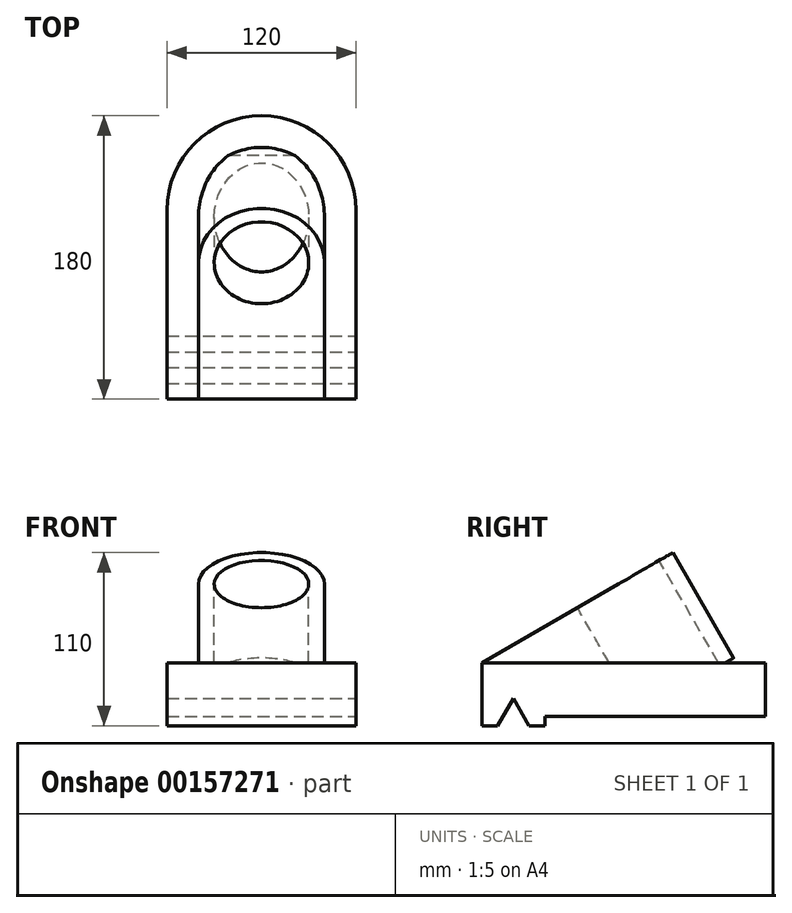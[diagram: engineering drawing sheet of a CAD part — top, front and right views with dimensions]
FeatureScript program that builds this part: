
annotation { "Feature Type Name" : "Feature", "Feature Type Description" : "" }
export const myFeature = defineFeature(function(context is Context, id is Id, definition is map)
    precondition{}
    {
        {
            var Q0;
            Q0=qCreatedBy(makeId("Front.planeOp"),FACE);
            var sketch = newSketch(context, id + "F0", { "sketchPlane" : qUnion([Q0])});
            skLineSegment(sketch, "E0", {"start": v(60, -20) * mm, "end": v(-60, -20) * mm});
            skLineSegment(sketch, "E1", {"start": v(-60, -20) * mm, "end": v(-60, 20) * mm});
            skLineSegment(sketch, "E2", {"start": v(-60, 20) * mm, "end": v(60, 20) * mm});
            skLineSegment(sketch, "E3", {"start": v(60, 20) * mm, "end": v(60, -20) * mm});
            skPoint(sketch, "E4.start.orphan", {"position": v(68, 0) * mm});
            skPoint(sketch, "E5.orphan", {"position": v(68, -20) * mm});
            skSolve(sketch);
        }
        {
            var Q0;
            Q0=makeQuery(id+"F0.imprint","IMPRINT",FACE,{"disambiguationData":[TD([[makeQuery(id+"F0.imprint","IMPRINT",EDGE,{"derivedFrom":sQuery(id+"F0.wireOp",EDGE,"E0")}),-1.0]])]});
            extrude(context, id + "F1", {"entities" : qUnion([Q0]), "oppositeDirection" : true, "depth" : 120 * mm});
        }
        {
            var Q0;
            Q0=makeQuery(id+"F1.opExtrude","SWEPT_FACE",FACE,{"disambiguationData":[OSD([sQuery(id+"F0.wireOp",EDGE,"E2")])]});
            var sketch = newSketch(context, id + "F2", { "sketchPlane" : qUnion([Q0])});
            skArc(sketch, "E6", {"start": v(60, 120) * mm, "mid": v(0, 180) * mm, "end": v(-60, 120) * mm});
            skSolve(sketch);
        }
        {
            var Q0;
            Q0=makeQuery(id+"F2.imprint","IMPRINT",FACE,{"disambiguationData":[TD([[makeQuery(id+"F2.imprint","IMPRINT",EDGE,{"derivedFrom":sQuery(id+"F2.wireOp",EDGE,"E6")}),1.0]])]});
            extrude(context, id + "F3", {"entities" : qUnion([Q0]), "operationType" : NewBodyOperationType.ADD, "oppositeDirection" : true, "depth" : 40 * mm});
        }
        {
            var Q0;
            Q0=makeQuery(id+"F1.opExtrude","CAP_EDGE",EDGE,{"disambiguationData":[OSD([sQuery(id+"F0.wireOp",EDGE,"E2")])],"isStart":true});
            cPlane(context, id + "F4", {"entities" : qUnion([Q0]), "cplaneType" : CPlaneType.LINE_ANGLE, "offset" : 25 * mm, "angle" : 120 * degree, "width" : 150 * mm, "height" : 150 * mm});
        }
        {
            var Q0;
            Q0=qCreatedBy(id+"F4.planeOp",FACE);
            var sketch = newSketch(context, id + "F5", { "sketchPlane" : qUnion([Q0])});
            skLineSegment(sketch, "E7", {"start": v(0, 10) * mm, "end": v(40, 10) * mm});
            skLineSegment(sketch, "E8", {"start": v(40, 10) * mm, "end": v(40, 110) * mm});
            skLineSegment(sketch, "E9", {"start": v(-40, 110) * mm, "end": v(-40, 10) * mm});
            skLineSegment(sketch, "E10", {"start": v(-40, 10) * mm, "end": v(0, 10) * mm});
            skCircle(sketch, "E11", {"center": v(0, 110) * mm, "radius": 40 * mm});
            skCircle(sketch, "E12", {"center": v(0, 110) * mm, "radius": 30 * mm});
            skSolve(sketch);
        }
        {
            var Q0;
            Q0=makeQuery(id+"F5.imprint","IMPRINT",FACE,{"disambiguationData":[TD([[makeQuery(id+"F5.imprint","IMPRINT",EDGE,{"derivedFrom":sQuery(id+"F5.wireOp",EDGE,"E7")}),1.0]])]});
            var Q1;
            Q1=makeQuery(id+"F5.imprint","IMPRINT",FACE,{"disambiguationData":[TD([[makeQuery(id+"F5.imprint","IMPRINT",EDGE,{"derivedFrom":sQuery(id+"F5.wireOp",EDGE,"E12")}),-1.0]])]});
            extrude(context, id + "F8", {"entities" : qUnion([Q0, Q1]), "operationType" : NewBodyOperationType.ADD, "oppositeDirection" : true, "depth" : 77.3 * mm});
        }
        {
            var Q0;
            Q0=makeQuery(id+"F1.opExtrude","SWEPT_FACE",FACE,{"disambiguationData":[OSD([sQuery(id+"F0.wireOp",EDGE,"E3")])]});
            var sketch = newSketch(context, id + "F9", { "sketchPlane" : qUnion([Q0])});
            skLineSegment(sketch, "E13.bottom", {"start": v(40, -20) * mm, "end": v(191.6, -20) * mm});
            skLineSegment(sketch, "E13.top", {"start": v(40, -14) * mm, "end": v(191.6, -14) * mm});
            skLineSegment(sketch, "E13.left", {"start": v(40, -20) * mm, "end": v(40, -14) * mm});
            skLineSegment(sketch, "E13.right", {"start": v(191.6, -20) * mm, "end": v(191.6, -14) * mm});
            skSolve(sketch);
        }
        {
            var Q0;
            {var subQ4=sQuery(id+"F9.wireOp",EDGE,"E13.left");Q0=makeQuery(id+"F9.imprint","IMPRINT",FACE,{"disambiguationData":[TD([[makeQuery(id+"F9.imprint","IMPRINT",EDGE,{"derivedFrom":subQ4}),-1.0]])]});}
            var Q1;
            {var subQ4=sQuery(id+"F9.wireOp",EDGE,"E13.right");Q1=makeQuery(id+"F9.imprint","IMPRINT",FACE,{"disambiguationData":[TD([[makeQuery(id+"F9.imprint","IMPRINT",EDGE,{"derivedFrom":subQ4}),1.0]])]});}
            extrude(context, id + "F10", {"entities" : qUnion([Q0, Q1]), "operationType" : NewBodyOperationType.REMOVE, "oppositeDirection" : true, "depth" : 120 * mm});
        }
        {
            var Q0;
            Q0=makeQuery(id+"F1.opExtrude","SWEPT_FACE",FACE,{"disambiguationData":[OSD([sQuery(id+"F0.wireOp",EDGE,"E3")])]});
            var sketch = newSketch(context, id + "F11", { "sketchPlane" : qUnion([Q0])});
            skLineSegment(sketch, "E14", {"start": v(20, -20) * mm, "end": v(10, -20) * mm});
            skLineSegment(sketch, "E15", {"start": v(10, -20) * mm, "end": v(26.92, 9.3) * mm});
            skLineSegment(sketch, "E16", {"start": v(20, -20) * mm, "end": v(30, -20) * mm});
            skLineSegment(sketch, "E17", {"start": v(30, -20) * mm, "end": v(12.2, 10.81) * mm});
            skLineSegment(sketch, "E18", {"start": v(20, -20) * mm, "end": v(20, 9.02) * mm});
            skSolve(sketch);
        }
        {
            var Q0;
            {var subQ0=sQuery(id+"F11.wireOp",EDGE,"E16");Q0=makeQuery(id+"F11.imprint","IMPRINT",FACE,{"disambiguationData":[TD([[makeQuery(id+"F11.imprint","IMPRINT",EDGE,{"derivedFrom":subQ0}),-1.0]])]});}
            var Q1;
            {var subQ0=sQuery(id+"F11.wireOp",EDGE,"E14");Q1=makeQuery(id+"F11.imprint","IMPRINT",FACE,{"disambiguationData":[TD([[makeQuery(id+"F11.imprint","IMPRINT",EDGE,{"derivedFrom":subQ0}),-1.0]])]});}
            extrude(context, id + "F6", {"entities" : qUnion([Q0, Q1]), "operationType" : NewBodyOperationType.REMOVE, "oppositeDirection" : true, "depth" : 120 * mm});
        }
        {
            var Q0;
            {var subQ1=sQuery(id+"F5.wireOp",EDGE,"E8");Q0=makeQuery(id+"F8.boolean.opBoolean","SPLIT",FACE,{"disambiguationData":[TD([makeQuery(id+"F1.opExtrude","SWEPT_FACE",FACE,{"disambiguationData":[OSD([sQuery(id+"F0.wireOp",EDGE,"E0")])]})])],"derivedFrom":makeQuery(id+"F8.opExtrude","SWEPT_FACE",FACE,{"disambiguationData":[OSD([subQ1])]})});}
            extrude(context, id + "F7", {"entities" : qUnion([Q0]), "operationType" : NewBodyOperationType.REMOVE, "oppositeDirection" : true, "depth" : 80 * mm});
        }
    });
